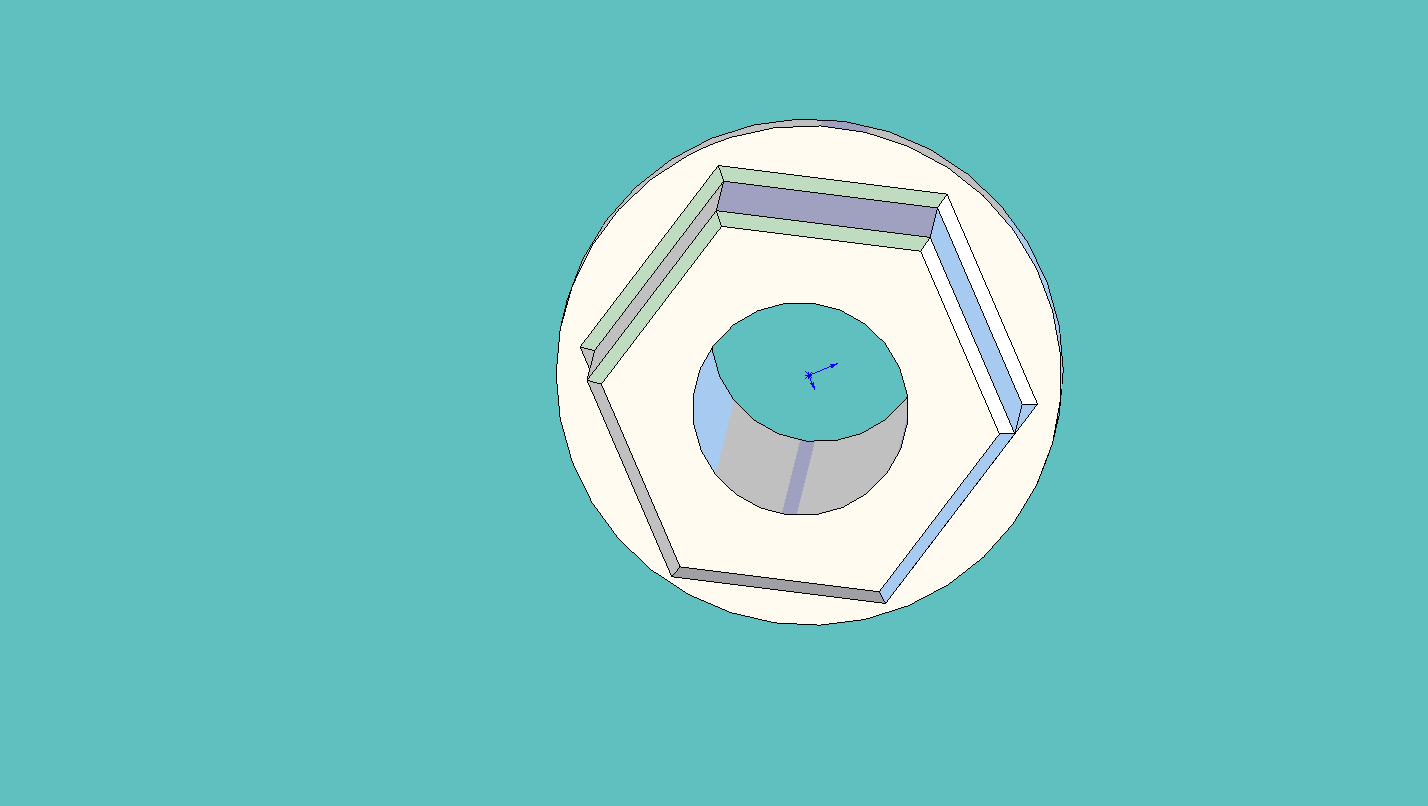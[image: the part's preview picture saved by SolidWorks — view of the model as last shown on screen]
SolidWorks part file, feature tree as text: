
SOLIDWORKS PART (.sldprt)
format: sldprt  version: not decoded by parser v0  size: 227,840 bytes
history: native  units: mm
features: sketch x4, extrude x3, chamfer x2, material x1, cut_extrude x1 (+13 scaffold rows collapsed)
feature tree (24):
  scaffold x13  (default folders/planes/origin — collapsed)
  material  "Material <not specified>"
  sketch  "Sketch2"
  extrude  "Extrude1"  Depth=12.7mm
  sketch  "Sketch3"
  extrude  "Extrude2"  Depth=2.54mm
  chamfer  "Chamfer1"  Distance=0.762mm Angle=45deg
  chamfer  "Chamfer2"  Distance=0.762mm Angle=45deg
  sketch  "Sketch5"
  extrude  "Extrude3"  Depth=12.7mm
  sketch  "Sketch4"
  cut_extrude  "Cut-Extrude1"  [1 undecoded]
decode coverage: 5 of 10 modeling features carry decoded parameters
note: 1 parameter value undecoded
note: suppression state not decoded; provenance and decode notes live in map.json
